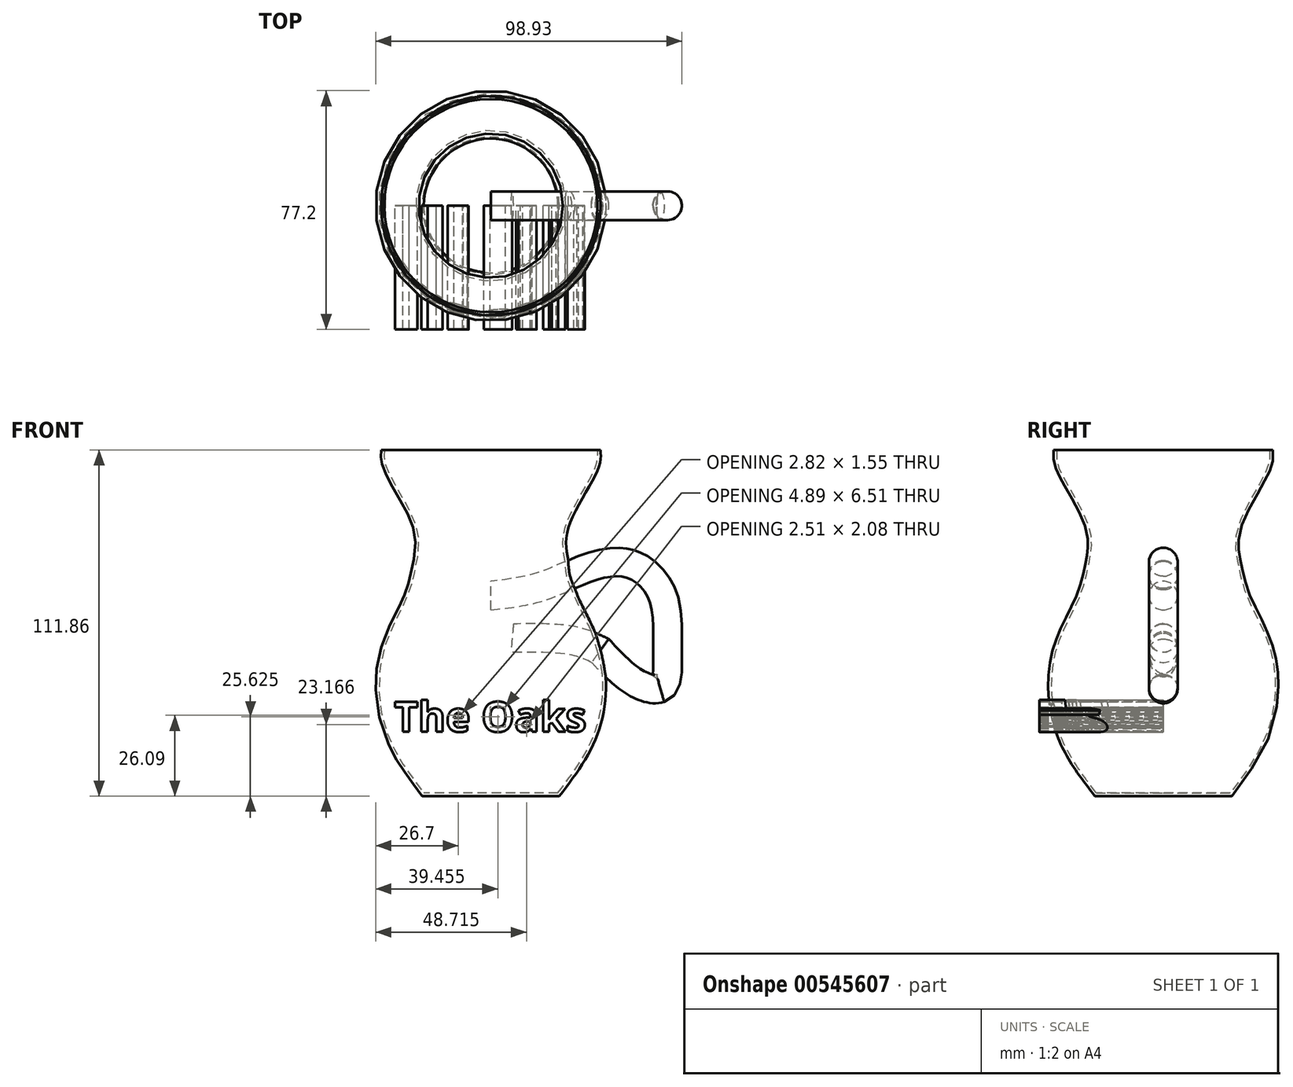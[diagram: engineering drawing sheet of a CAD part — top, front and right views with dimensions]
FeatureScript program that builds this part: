
annotation { "Feature Type Name" : "Feature", "Feature Type Description" : "" }
export const myFeature = defineFeature(function(context is Context, id is Id, definition is map)
    precondition{}
    {
        {
            var Q0;
            Q0=qCreatedBy(makeId("Front.planeOp"),FACE);
            var sketch = newSketch(context, id + "F0", { "sketchPlane" : qUnion([Q0])});
            skLineSegment(sketch, "E0", {"start": v(0, -64.83) * mm, "end": v(-22.17, -64.83) * mm});
            skFitSpline(sketch, "E1", {"points": [v(-22.17, -64.83) * mm, v(-34.92, -43.57) * mm, v(-35.72, -17.54) * mm, v(-28.01, 0) * mm, v(-25.09, 10.9) * mm, v(-25.09, 22.05) * mm, v(-34.65, 40.92) * mm, v(-35.45, 47.03) * mm], "startDerivative": vector(-85.72, 112.38) * mm, "endDerivative": vector(3.85, 59.3) * mm});
            skLineSegment(sketch, "E2", {"start": v(-35.45, 47.03) * mm, "end": v(0, 47.03) * mm});
            skLineSegment(sketch, "E3", {"start": v(0, 47.03) * mm, "end": v(0, -64.83) * mm});
            skSolve(sketch);
        }
        {
            var Q0;
            Q0=makeQuery(id+"F0.imprint","IMPRINT",FACE,{"disambiguationData":[TD([[makeQuery(id+"F0.imprint","IMPRINT",EDGE,{"derivedFrom":sQuery(id+"F0.wireOp",EDGE,"E0")}),-1.0]])]});
            var Q1;
            Q1=sQuery(id+"F0.wireOp",EDGE,"E3");
            revolve(context, id + "F1", {"entities" : qUnion([Q0]), "axis" : qUnion([Q1]), "revolveType" : RevolveType.FULL});
        }
        {
            var Q0;
            Q0=makeQuery(id+"F1.opRevolve","SWEPT_FACE",FACE,{"disambiguationData":[OSD([sQuery(id+"F0.wireOp",EDGE,"E2")])]});
            shell(context, id + "F2", {"entities" : qUnion([Q0]), "thickness" : 1 * mm});
        }
        {
            var Q0;
            Q0=qCreatedBy(makeId("Right.planeOp"),FACE);
            var sketch = newSketch(context, id + "F3", { "sketchPlane" : qUnion([Q0])});
            skCircle(sketch, "E4", {"center": v(0, 0) * mm, "radius": 4.64 * mm});
            skSolve(sketch);
        }
        {
            var Q0;
            Q0=qCreatedBy(makeId("Front.planeOp"),FACE);
            var sketch = newSketch(context, id + "F4", { "sketchPlane" : qUnion([Q0])});
            skFitSpline(sketch, "E5", {"points": [v(0, 0) * mm, v(16, 2.86) * mm, v(32.17, 9.22) * mm, v(45.7, 10.02) * mm, v(55.5, 0) * mm, v(57.1, -18.62) * mm, v(55.5, -29.49) * mm, v(47.28, -28.43) * mm, v(35.35, -17.82) * mm], "startDerivative": vector(120.13, 13.37) * mm, "endDerivative": vector(-85.92, 93.46) * mm});
            skFitSpline(sketch, "E6", {"points": [v(35.35, -17.82) * mm, v(26.25, -14.58) * mm, v(6.9, -13.79) * mm], "startDerivative": vector(-19.7, 9.16) * mm, "endDerivative": vector(-36.26, -0.54) * mm});
            skSolve(sketch);
        }
        {
            var Q0;
            Q0 = qSketchRegion(id + "F3", true);
            var Q1;
            Q1 = qConstructionFilter(qBodyType(qCreatedBy(id + "F4" ,EDGE), BodyType.WIRE), ConstructionObject.NO);
            sweep(context, id + "F5", {"operationType" : NewBodyOperationType.ADD, "profiles" : qUnion([Q0]), "path" : qUnion([Q1])});
        }
        {
            var Q0;
            Q0=qCreatedBy(makeId("Front.planeOp"),FACE);
            var sketch = newSketch(context, id + "F6", { "sketchPlane" : qUnion([Q0])});
            skText(sketch, "E7", { "text": "The Oaks", "fontName": "OpenSans-Bold.ttf"});
            const initialGuessF6  = {"E7": [-0.03127, -0.04404, 1, 0, 0.00972]};
            skSetInitialGuess(sketch, initialGuessF6);
            skSolve(sketch);
        }
        {
            var Q0;
            Q0 = qSketchRegion(id + "F6", true);
            extrude(context, id + "F7", {"entities" : qUnion([Q0]), "operationType" : NewBodyOperationType.ADD, "depth" : 40 * mm, "offsetDistance" : 25 * mm});
        }
    });
